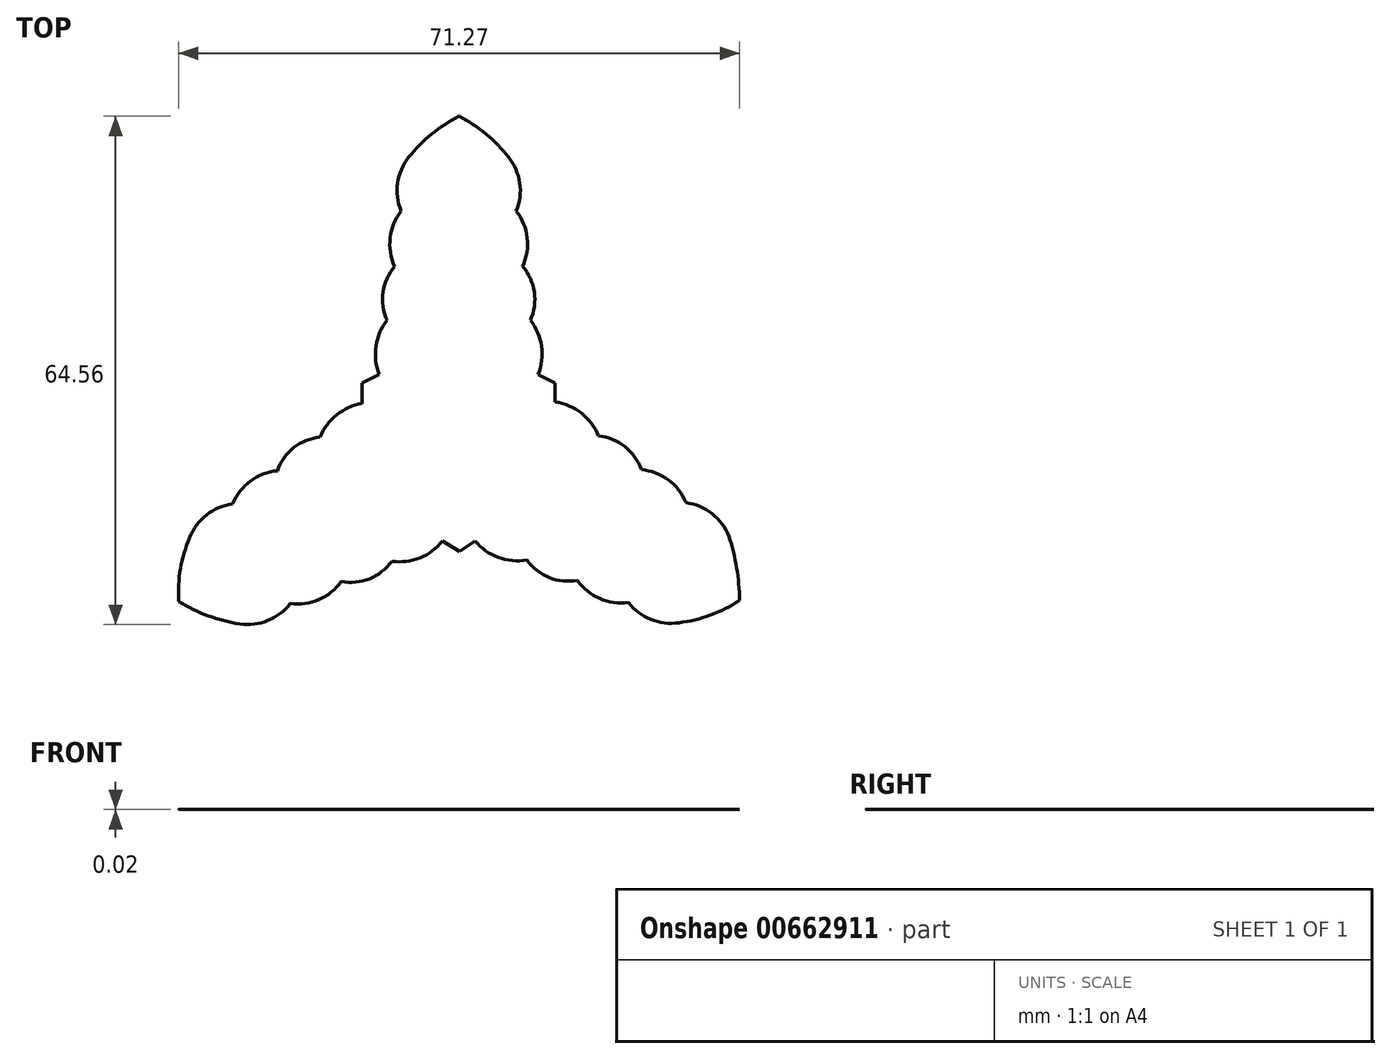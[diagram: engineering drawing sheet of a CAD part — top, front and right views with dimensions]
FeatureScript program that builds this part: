
annotation { "Feature Type Name" : "Feature", "Feature Type Description" : "" }
export const myFeature = defineFeature(function(context is Context, id is Id, definition is map)
    precondition{}
    {
        {
            var Q0;
            Q0=qCreatedBy(makeId("Top.planeOp"),FACE);
            var sketch = newSketch(context, id + "F0", { "sketchPlane" : qUnion([Q0])});
            skPoint(sketch, "E0.center", {"position": v(0, 0) * mm});
            skArc(sketch, "E1", {"start": v(-6.45, 35.84) * mm, "mid": v(-7.87, 32.54) * mm, "end": v(-7.42, 28.98) * mm});
            skArc(sketch, "E2", {"start": v(-7.42, 28.98) * mm, "mid": v(-8.81, 25.6) * mm, "end": v(-8.23, 21.98) * mm});
            skArc(sketch, "E3", {"start": v(-8.23, 21.98) * mm, "mid": v(-9.72, 18.7) * mm, "end": v(-9.2, 15.13) * mm});
            skArc(sketch, "E4", {"start": v(-9.2, 15.13) * mm, "mid": v(-10.62, 11.82) * mm, "end": v(-10.2, 8.25) * mm});
            skLineSegment(sketch, "E5", {"start": v(-10.2, 8.25) * mm, "end": v(-12.37, 7.15) * mm});
            skLineSegment(sketch, "E6", {"start": v(-12.37, 7.15) * mm, "end": v(-12.37, 4.64) * mm});
            skLineSegment(sketch, "E7.MirrorCS", {"start": v(12.16, 7.15) * mm, "end": v(12.16, 4.64) * mm});
            skLineSegment(sketch, "E8.MirrorCS", {"start": v(10, 8.25) * mm, "end": v(12.16, 7.15) * mm});
            skArc(sketch, "E9.MirrorCS", {"start": v(9, 15.13) * mm, "mid": v(10.4, 11.82) * mm, "end": v(10, 8.25) * mm});
            skArc(sketch, "E10.MirrorCS", {"start": v(8.01, 21.98) * mm, "mid": v(9.5, 18.7) * mm, "end": v(9, 15.13) * mm});
            skArc(sketch, "E11.MirrorCS", {"start": v(7.2, 28.98) * mm, "mid": v(8.6, 25.6) * mm, "end": v(8.01, 21.98) * mm});
            skArc(sketch, "E12.MirrorCS", {"start": v(6.23, 35.84) * mm, "mid": v(7.66, 32.54) * mm, "end": v(7.2, 28.98) * mm});
            skArc(sketch, "E13", {"start": v(34.22, -12.32) * mm, "mid": v(32.07, -9.44) * mm, "end": v(28.76, -8.05) * mm});
            skArc(sketch, "E14", {"start": v(28.76, -8.05) * mm, "mid": v(26.53, -5.15) * mm, "end": v(23.1, -3.85) * mm});
            skArc(sketch, "E15", {"start": v(23.1, -3.85) * mm, "mid": v(21, -0.92) * mm, "end": v(17.66, 0.43) * mm});
            skArc(sketch, "E16", {"start": v(17.66, 0.43) * mm, "mid": v(15.48, 3.32) * mm, "end": v(12.16, 4.74) * mm});
            skArc(sketch, "E17.MirrorCS", {"start": v(8.56, -15.34) * mm, "mid": v(4.94, -15) * mm, "end": v(1.97, -12.9) * mm});
            skArc(sketch, "E18.MirrorCS", {"start": v(14.98, -17.91) * mm, "mid": v(11.4, -17.56) * mm, "end": v(8.56, -15.34) * mm});
            skArc(sketch, "E19.MirrorCS", {"start": v(21.45, -20.71) * mm, "mid": v(17.82, -20.23) * mm, "end": v(14.98, -17.91) * mm});
            skArc(sketch, "E20.MirrorCS", {"start": v(27.87, -23.3) * mm, "mid": v(24.3, -22.89) * mm, "end": v(21.45, -20.71) * mm});
            skLineSegment(sketch, "E21", {"start": v(1.97, -12.9) * mm, "end": v(0, -14.26) * mm});
            skLineSegment(sketch, "E22", {"start": v(0, -14.26) * mm, "end": v(-2.14, -12.9) * mm});
            skArc(sketch, "E23", {"start": v(-27.91, -23.45) * mm, "mid": v(-24.35, -23.03) * mm, "end": v(-21.5, -20.86) * mm});
            skArc(sketch, "E24", {"start": v(-21.5, -20.86) * mm, "mid": v(-17.86, -20.37) * mm, "end": v(-15.02, -18.05) * mm});
            skArc(sketch, "E25", {"start": v(-15.02, -18.05) * mm, "mid": v(-11.43, -17.7) * mm, "end": v(-8.6, -15.48) * mm});
            skArc(sketch, "E26", {"start": v(-8.6, -15.48) * mm, "mid": v(-5.03, -15.05) * mm, "end": v(-2.14, -12.9) * mm});
            skArc(sketch, "E27.MirrorCS", {"start": v(-17.7, 0.28) * mm, "mid": v(-15.6, 3.12) * mm, "end": v(-12.37, 4.57) * mm});
            skArc(sketch, "E28.MirrorCS", {"start": v(-23.14, -4) * mm, "mid": v(-21.05, -1.06) * mm, "end": v(-17.7, 0.28) * mm});
            skArc(sketch, "E29.MirrorCS", {"start": v(-28.8, -8.2) * mm, "mid": v(-26.56, -5.3) * mm, "end": v(-23.14, -4) * mm});
            skArc(sketch, "E30.MirrorCS", {"start": v(-34.25, -12.46) * mm, "mid": v(-32.11, -9.58) * mm, "end": v(-28.8, -8.2) * mm});
            skLineSegment(sketch, "E31", {"start": v(-12.37, 4.64) * mm, "end": v(-12.37, 4.57) * mm});
            skArc(sketch, "E32", {"start": v(-0.06, 41.04) * mm, "mid": v(-3.54, 38.79) * mm, "end": v(-6.45, 35.84) * mm});
            skArc(sketch, "E33", {"start": v(6.23, 35.84) * mm, "mid": v(3.38, 38.8) * mm, "end": v(-0.06, 41.04) * mm});
            skArc(sketch, "E34", {"start": v(-34.25, -12.46) * mm, "mid": v(-35.45, -16.43) * mm, "end": v(-35.66, -20.56) * mm});
            skArc(sketch, "E35", {"start": v(-35.66, -20.56) * mm, "mid": v(-31.94, -22.42) * mm, "end": v(-27.91, -23.45) * mm});
            skArc(sketch, "E36", {"start": v(35.57, -20.47) * mm, "mid": v(35.2, -16.34) * mm, "end": v(34.22, -12.32) * mm});
            skArc(sketch, "E37", {"start": v(27.87, -23.3) * mm, "mid": v(31.88, -22.33) * mm, "end": v(35.57, -20.47) * mm});
            skSolve(sketch);
        }
        {
            var Q0;
            Q0=makeQuery(id+"F0.imprint","IMPRINT",FACE,{"disambiguationData":[TD([[makeQuery(id+"F0.imprint","IMPRINT",EDGE,{"derivedFrom":sQuery(id+"F0.wireOp",EDGE,"E1")}),1.0]])]});
            extrude(context, id + "F1", {"entities" : qUnion([Q0]), "depth" : 9 / 406.4 * mm, "offsetDistance" : 25.4 * mm});
        }
    });
